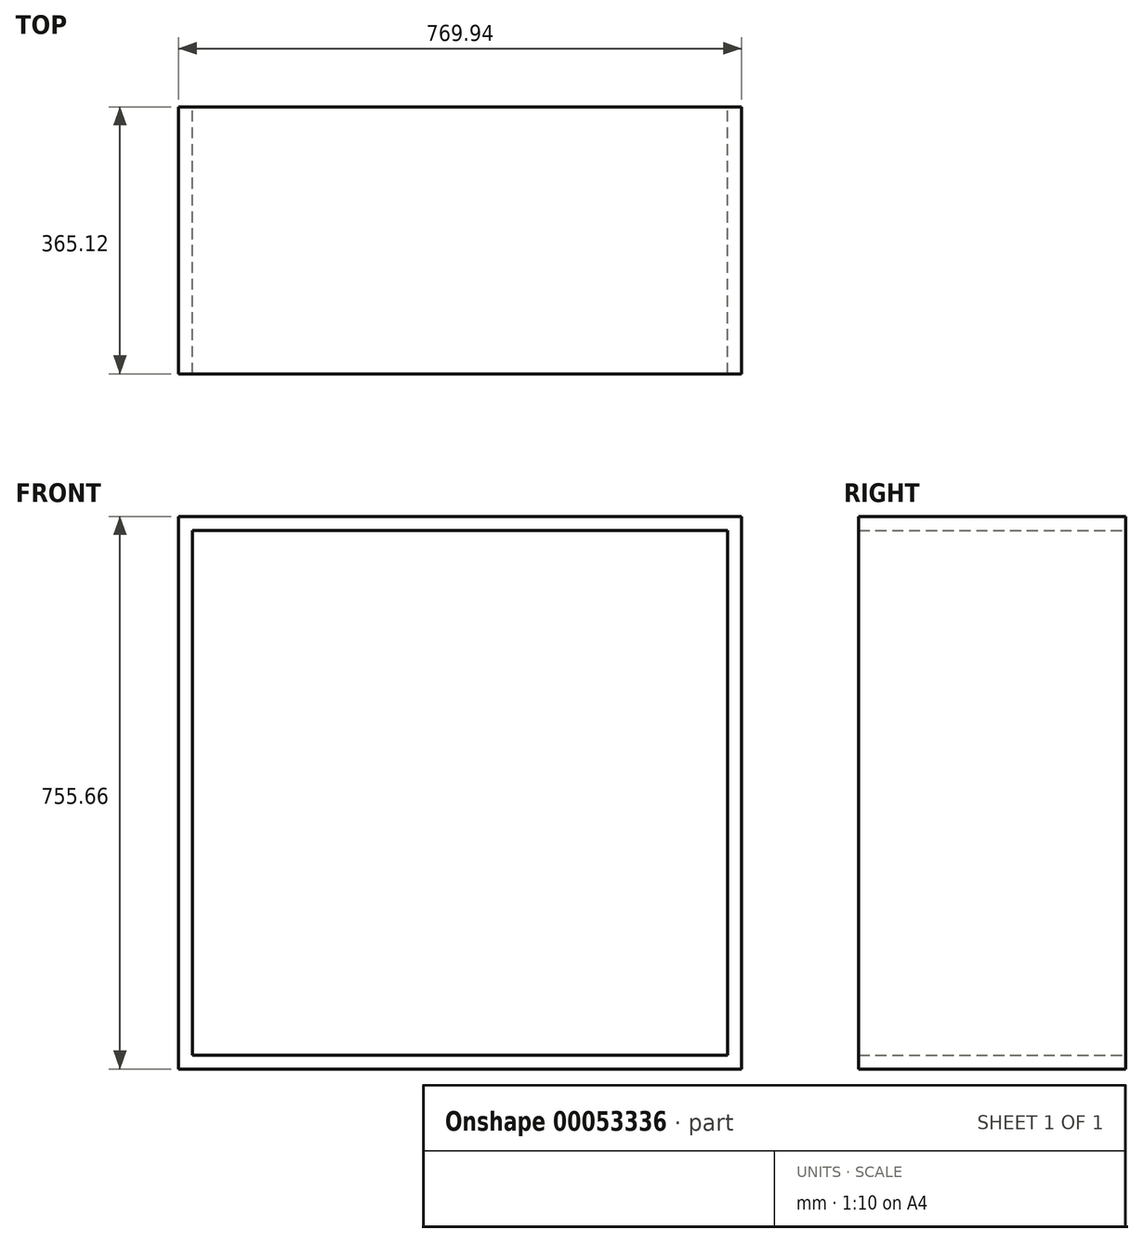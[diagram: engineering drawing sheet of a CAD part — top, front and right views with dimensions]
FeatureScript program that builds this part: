
annotation { "Feature Type Name" : "Feature", "Feature Type Description" : "" }
export const myFeature = defineFeature(function(context is Context, id is Id, definition is map)
    precondition{}
    {
        {
            var Q0;
            Q0=qCreatedBy(makeId("Front.planeOp"),FACE);
            var sketch = newSketch(context, id + "F0", { "sketchPlane" : qUnion([Q0])});
            skLineSegment(sketch, "E0.rect.bottom", {"start": v(-384.97, -377.83) * mm, "end": v(384.97, -377.83) * mm});
            skLineSegment(sketch, "E0.rect.top", {"start": v(-384.97, 377.82) * mm, "end": v(384.97, 377.82) * mm});
            skLineSegment(sketch, "E0.rect.left", {"start": v(-384.97, -377.83) * mm, "end": v(-384.97, 377.82) * mm});
            skLineSegment(sketch, "E0.rect.right", {"start": v(384.97, -377.83) * mm, "end": v(384.97, 377.82) * mm});
            skPoint(sketch, "E0.rect.middle", {"position": v(0, 0) * mm});
            skSolve(sketch);
        }
        {
            var Q0;
            Q0=makeQuery(id+"F0.imprint","IMPRINT",FACE,{"disambiguationData":[TD([[makeQuery(id+"F0.imprint","IMPRINT",EDGE,{"derivedFrom":sQuery(id+"F0.wireOp",EDGE,"E0.rect.bottom")}),1.0]])]});
            var sketch = newSketch(context, id + "F1", { "sketchPlane" : qUnion([Q0])});
            skLineSegment(sketch, "E1.rect.bottom", {"start": v(-365.91, 358.78) * mm, "end": v(365.91, 358.78) * mm});
            skLineSegment(sketch, "E1.rect.top", {"start": v(-365.91, -358.78) * mm, "end": v(365.91, -358.78) * mm});
            skLineSegment(sketch, "E1.rect.left", {"start": v(-365.91, 358.78) * mm, "end": v(-365.91, -358.78) * mm});
            skLineSegment(sketch, "E1.rect.right", {"start": v(365.91, 358.78) * mm, "end": v(365.91, -358.78) * mm});
            skPoint(sketch, "E1.rect.middle", {"position": v(0, 0) * mm});
            skSolve(sketch);
        }
        {
            var Q0;
            Q0=makeQuery(id+"F1.imprint","IMPRINT",FACE,{"disambiguationData":[TD([[makeQuery(id+"F1.imprint","IMPRINT",EDGE,{"derivedFrom":sQuery(id+"F1.wireOp",EDGE,"E1.rect.bottom")}),1.0]])]});
            extrude(context, id + "F2", {"entities" : qUnion([Q0]), "endBound" : BoundingType.SYMMETRIC, "depth" : 365.12 * mm});
        }
    });
